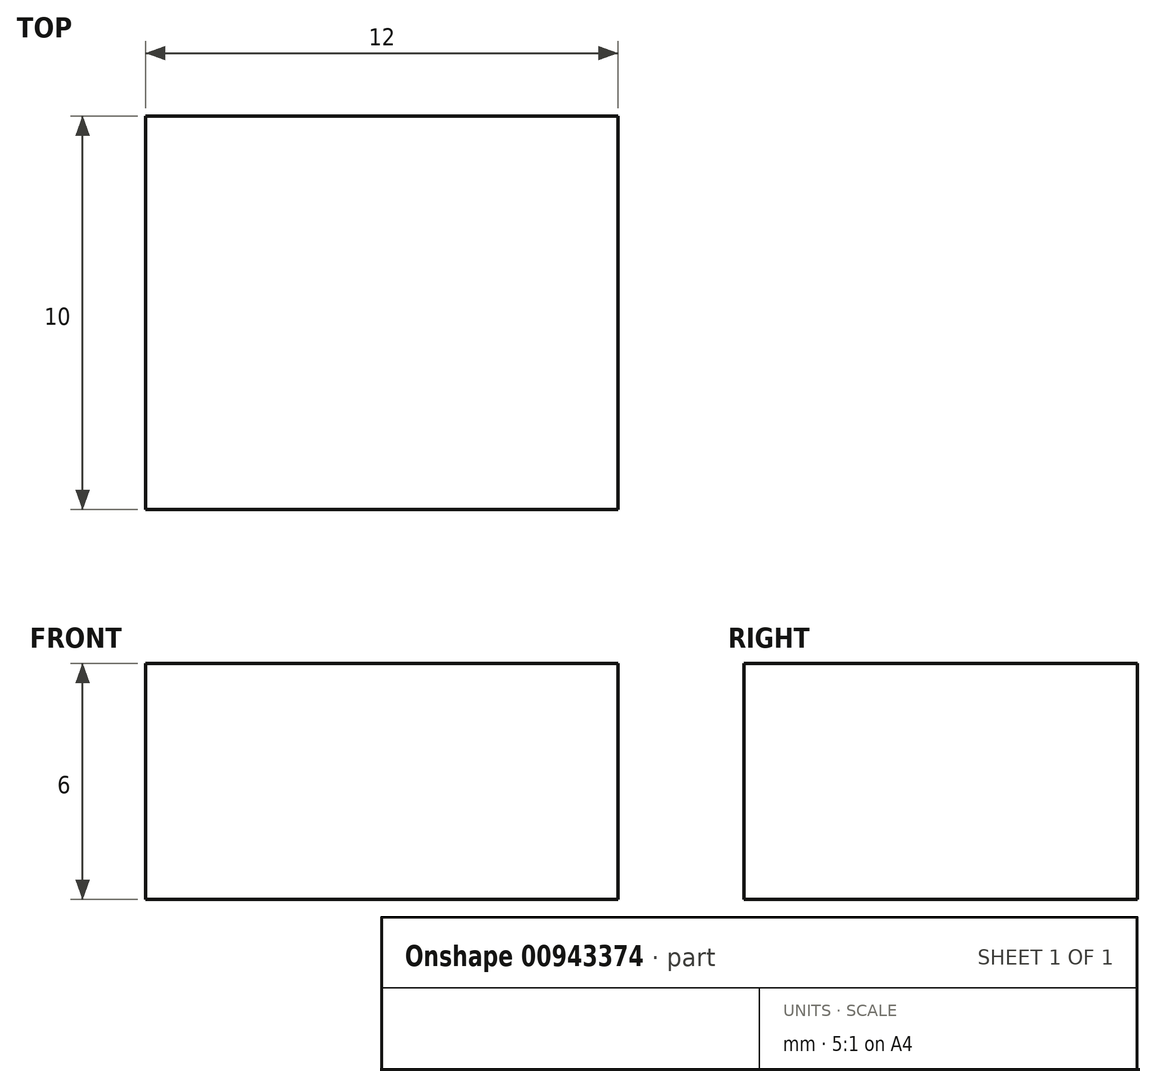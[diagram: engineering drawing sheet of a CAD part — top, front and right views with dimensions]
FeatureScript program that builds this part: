
annotation { "Feature Type Name" : "Feature", "Feature Type Description" : "" }
export const myFeature = defineFeature(function(context is Context, id is Id, definition is map)
    precondition{}
    {
        {
            var Q0;
            Q0=qCreatedBy(makeId("Front.planeOp"),FACE);
            var sketch = newSketch(context, id + "F0", { "sketchPlane" : qUnion([Q0])});
            skLineSegment(sketch, "E0.bottom", {"start": v(6, 3) * mm, "end": v(-6, 3) * mm});
            skLineSegment(sketch, "E0.top", {"start": v(6, -3) * mm, "end": v(-6, -3) * mm});
            skLineSegment(sketch, "E0.left", {"start": v(6, 3) * mm, "end": v(6, -3) * mm});
            skLineSegment(sketch, "E0.right", {"start": v(-6, 3) * mm, "end": v(-6, -3) * mm});
            skPoint(sketch, "E0.middle", {"position": v(0, 0) * mm});
            skSolve(sketch);
        }
        {
            var Q0;
            Q0=makeQuery(id+"F0.imprint","IMPRINT",FACE,{"disambiguationData":[TD([[makeQuery(id+"F0.imprint","IMPRINT",EDGE,{"derivedFrom":sQuery(id+"F0.wireOp",EDGE,"E0.bottom")}),1.0]])]});
            extrude(context, id + "F1", {"entities" : qUnion([Q0]), "endBound" : BoundingType.SYMMETRIC, "depth" : 10 * mm, "offsetDistance" : 25 * mm});
        }
    });
